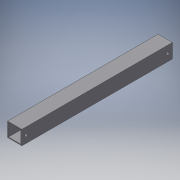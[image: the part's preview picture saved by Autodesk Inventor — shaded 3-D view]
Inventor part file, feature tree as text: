
AUTODESK INVENTOR PART (.ipt)
format: ipt  version: 2018 (Build 220112000, 112)  size: 113,664 bytes
history: native  units: in
note: dims shown in document units (in); Inventor stores cm internally (conversion verified against a paired STEP export)
features: extrude x2, sketch x2
ambient origin geometry x8: Origin, YZ Plane, XZ Plane, XY Plane, X Axis, Y Axis, Z Axis, Center Point
bodies: Solid1 (feature_tree)
feature tree (4):
  extrude  "Extrusion1"  Depth=1.0in
  extrude  "Extrusion2"  Depth=0.065in
  sketch  "Sketch1"  dims[d0=1.0in d1=1.0in]
  sketch  "Sketch2"  dims[d2=0.065in d3=0.065in d4=10.5in d5=0.0in d6=9.878in d7=0.2in d8=0.2in d11=0.1in d12=0.0in d15=0.5in d16=0.5in d17=0.3in]
